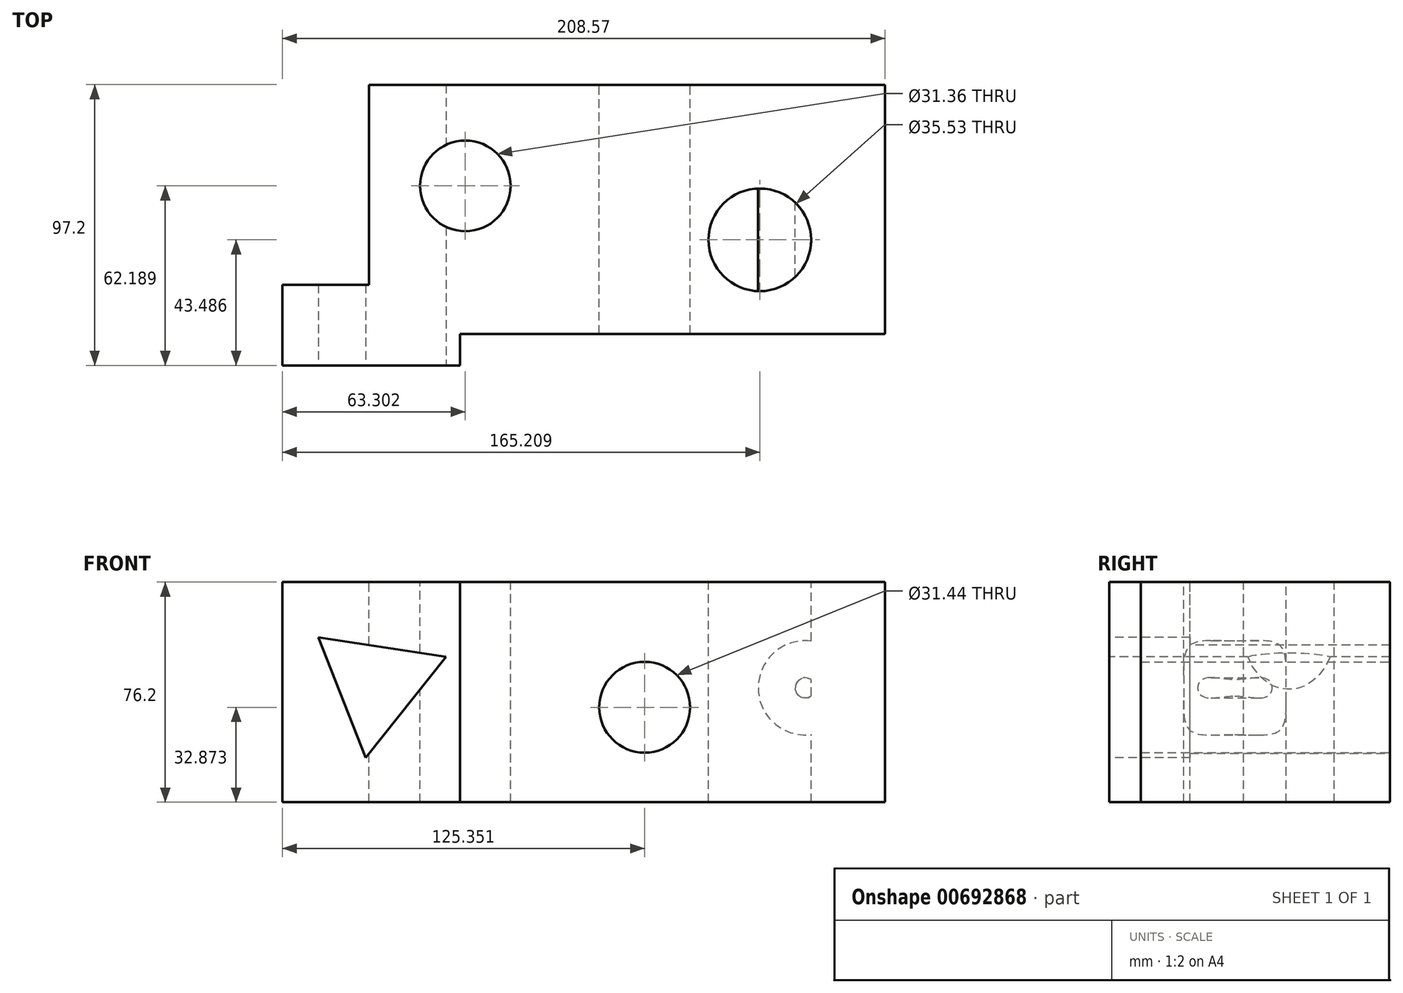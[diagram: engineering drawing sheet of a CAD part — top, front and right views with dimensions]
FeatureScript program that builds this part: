
annotation { "Feature Type Name" : "Feature", "Feature Type Description" : "" }
export const myFeature = defineFeature(function(context is Context, id is Id, definition is map)
    precondition{}
    {
        {
            var Q0;
            Q0=qCreatedBy(makeId("Top.planeOp"),FACE);
            var sketch = newSketch(context, id + "F0", { "sketchPlane" : qUnion([Q0])});
            skLineSegment(sketch, "E0.bottom", {"start": v(-72.62, 26.88) * mm, "end": v(105.98, 26.88) * mm});
            skLineSegment(sketch, "E0.top", {"start": v(-41.13, -59.37) * mm, "end": v(105.98, -59.37) * mm});
            skLineSegment(sketch, "E0.left", {"start": v(-72.62, 26.88) * mm, "end": v(-72.62, -42.35) * mm});
            skLineSegment(sketch, "E0.right", {"start": v(105.98, 26.88) * mm, "end": v(105.98, -59.37) * mm});
            skCircle(sketch, "E1", {"center": v(-39.29, -8.13) * mm, "radius": 15.68 * mm});
            skCircle(sketch, "E2", {"center": v(62.62, -26.83) * mm, "radius": 17.77 * mm});
            skLineSegment(sketch, "E3.bottom", {"start": v(-102.6, -42.35) * mm, "end": v(-72.62, -42.35) * mm});
            skLineSegment(sketch, "E3.top", {"start": v(-102.6, -70.32) * mm, "end": v(-41.13, -70.32) * mm});
            skLineSegment(sketch, "E3.left", {"start": v(-102.6, -42.35) * mm, "end": v(-102.6, -70.32) * mm});
            skLineSegment(sketch, "E3.right", {"start": v(-41.13, -59.37) * mm, "end": v(-41.13, -70.32) * mm});
            skLineSegment(sketch, "E4", {"start": v(-21.04, 36.25) * mm, "end": v(-51.18, 36.25) * mm, "construction": true});
            skSolve(sketch);
        }
        {
            var Q0;
            Q0 = qSketchRegion(id + "F0", true);
            extrude(context, id + "F1", {"entities" : qUnion([Q0]), "oppositeDirection" : true, "depth" : 76.2 * mm, "offsetDistance" : 25.4 * mm});
        }
        {
            var Q0;
            Q0=makeQuery(id+"F1.opExtrude","SWEPT_FACE",FACE,{"disambiguationData":[OSD([sQuery(id+"F0.wireOp",EDGE,"E3.top")])]});
            var sketch = newSketch(context, id + "F2", { "sketchPlane" : qUnion([Q0])});
            skCircle(sketch, "E5.cCircle", {"center": v(-69.93, -35.23) * mm, "radius": 12.9 * mm, "construction": true});
            skLineSegment(sketch, "E5.0", {"start": v(-45.9, -25.8) * mm, "end": v(-73.78, -60.75) * mm});
            skLineSegment(sketch, "E5.1", {"start": v(-73.78, -60.75) * mm, "end": v(-90.1, -19.14) * mm});
            skLineSegment(sketch, "E5.2", {"start": v(-90.1, -19.14) * mm, "end": v(-45.9, -25.8) * mm});
            skPoint(sketch, "E5.0.midPoint", {"position": v(-59.84, -43.28) * mm});
            skSolve(sketch);
        }
        {
            var Q0;
            Q0=makeQuery(id+"F2.imprint","IMPRINT",FACE,{"disambiguationData":[TD([[makeQuery(id+"F2.imprint","IMPRINT",EDGE,{"derivedFrom":sQuery(id+"F2.wireOp",EDGE,"E5.0")}),-1.0]])]});
            extrude(context, id + "F3", {"entities" : qUnion([Q0]), "operationType" : NewBodyOperationType.REMOVE, "oppositeDirection" : true, "depth" : 112.52 * mm, "offsetDistance" : 25.4 * mm});
        }
        {
            var Q0;
            Q0=makeQuery(id+"F1.opExtrude","SWEPT_FACE",FACE,{"disambiguationData":[OSD([sQuery(id+"F0.wireOp",EDGE,"E0.bottom")])]});
            var sketch = newSketch(context, id + "F4", { "sketchPlane" : qUnion([Q0])});
            skCircle(sketch, "E6", {"center": v(-22.76, -43.33) * mm, "radius": 15.72 * mm});
            skSolve(sketch);
        }
        {
            var Q0;
            Q0 = qSketchRegion(id + "F4", true);
            extrude(context, id + "F5", {"entities" : qUnion([Q0]), "operationType" : NewBodyOperationType.REMOVE, "oppositeDirection" : true, "depth" : 182.63 * mm, "offsetDistance" : 25.4 * mm});
        }
        {
            var Q0;
            Q0=makeQuery(id+"F1.opExtrude","SWEPT_FACE",FACE,{"disambiguationData":[OSD([sQuery(id+"F0.wireOp",EDGE,"E0.bottom")])]});
            var sketch = newSketch(context, id + "F6", { "sketchPlane" : qUnion([Q0])});
            skCircle(sketch, "E7", {"center": v(-78.34, -36.6) * mm, "radius": 3.5 * mm});
            skCircle(sketch, "E8", {"center": v(-78.34, -36.6) * mm, "radius": 16.33 * mm});
            skSolve(sketch);
        }
        {
            var Q0;
            Q0 = qSketchRegion(id + "F6", true);
            extrude(context, id + "F7", {"entities" : qUnion([Q0]), "operationType" : NewBodyOperationType.ADD, "oppositeDirection" : true, "depth" : 86.1 * mm, "offsetDistance" : 25.4 * mm});
        }
    });
